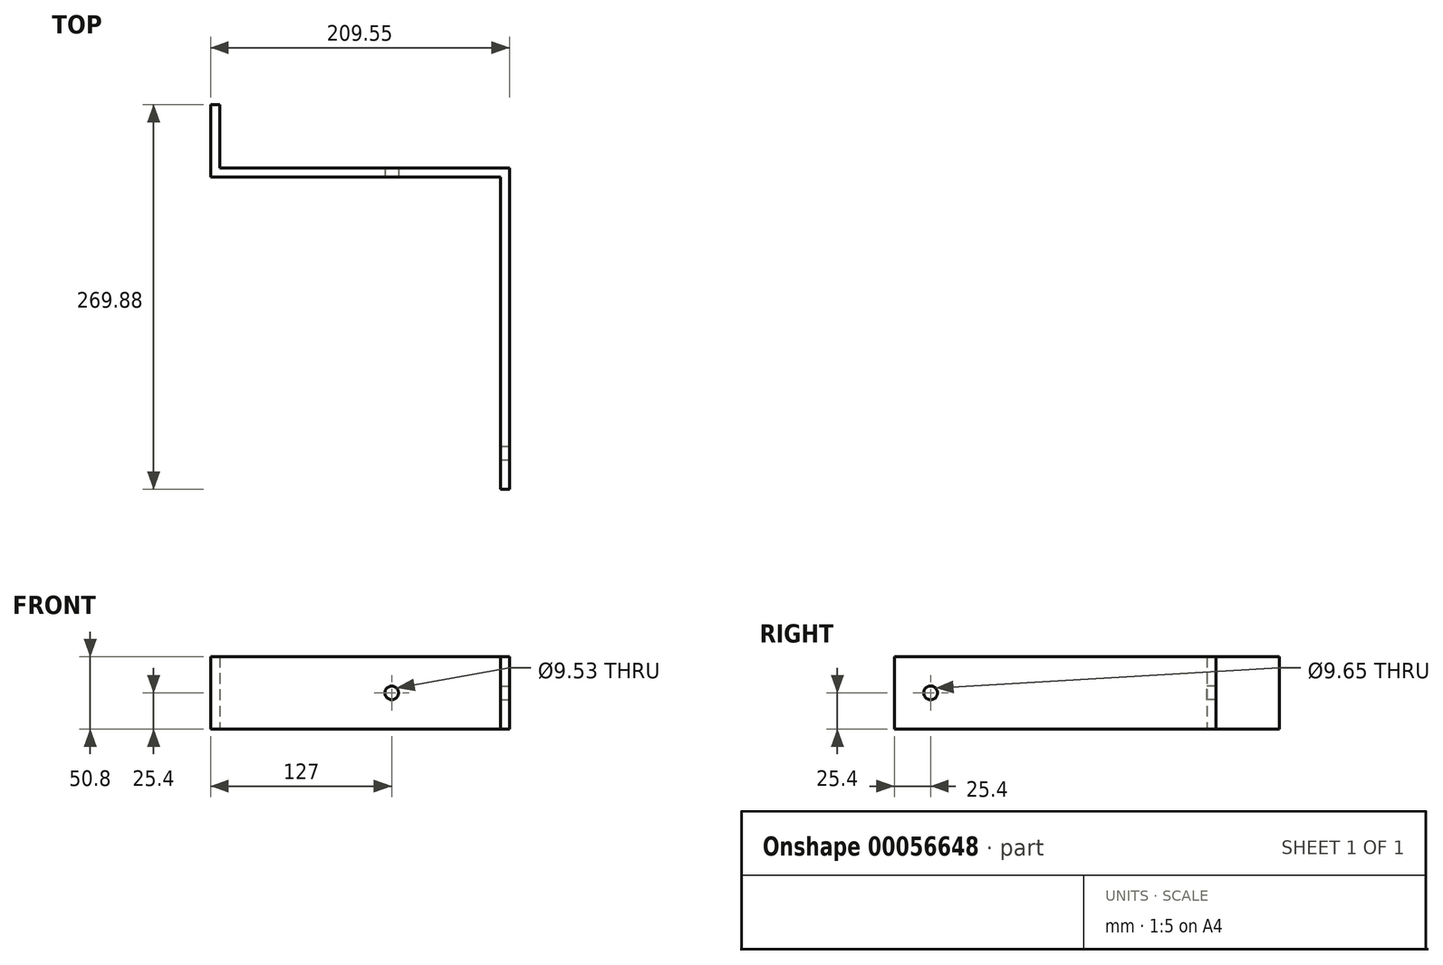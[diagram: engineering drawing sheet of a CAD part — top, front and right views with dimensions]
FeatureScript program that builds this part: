
annotation { "Feature Type Name" : "Feature", "Feature Type Description" : "" }
export const myFeature = defineFeature(function(context is Context, id is Id, definition is map)
    precondition{}
    {
        {
            var Q0;
            Q0=qCreatedBy(makeId("Top.planeOp"),FACE);
            var sketch = newSketch(context, id + "F0", { "sketchPlane" : qUnion([Q0])});
            skLineSegment(sketch, "E0", {"start": v(-6.35, 0) * mm, "end": v(-6.35, 219.08) * mm});
            skLineSegment(sketch, "E1", {"start": v(0, 225.43) * mm, "end": v(0, 0) * mm});
            skLineSegment(sketch, "E2", {"start": v(0, 225.43) * mm, "end": v(-203.2, 225.43) * mm});
            skLineSegment(sketch, "E3", {"start": v(-203.2, 225.42) * mm, "end": v(-203.2, 269.88) * mm});
            skLineSegment(sketch, "E4", {"start": v(-203.2, 269.88) * mm, "end": v(-209.55, 269.88) * mm});
            skLineSegment(sketch, "E5", {"start": v(-209.55, 269.88) * mm, "end": v(-209.55, 219.07) * mm});
            skLineSegment(sketch, "E6", {"start": v(-6.35, 219.08) * mm, "end": v(-209.55, 219.07) * mm});
            skLineSegment(sketch, "E7", {"start": v(-6.35, 0) * mm, "end": v(0, 0) * mm});
            skSolve(sketch);
        }
        {
            var Q0;
            Q0=qSketchRegion(id+"F0",true);
            extrude(context, id + "F1", {"entities" : qUnion([Q0]), "endBound" : BoundingType.SYMMETRIC, "depth" : 50.8 * mm});
        }
        {
            var Q0;
            Q0=makeQuery(id+"F1.opExtrude","SWEPT_FACE",FACE,{"disambiguationData":[OSD([sQuery(id+"F0.wireOp",EDGE,"E6")])]});
            var sketch = newSketch(context, id + "F2", { "sketchPlane" : qUnion([Q0])});
            skCircle(sketch, "E8", {"center": v(-82.55, 0) * mm, "radius": 4.76 * mm});
            skSolve(sketch);
        }
        {
            var Q0;
            Q0=qSketchRegion(id+"F2",true);
            extrude(context, id + "F3", {"entities" : qUnion([Q0]), "operationType" : NewBodyOperationType.REMOVE, "endBound" : BoundingType.THROUGH_ALL, "oppositeDirection" : true, "depth" : 25.4 * mm});
        }
        {
            var Q0;
            Q0=makeQuery(id+"F1.opExtrude","SWEPT_FACE",FACE,{"disambiguationData":[OSD([sQuery(id+"F0.wireOp",EDGE,"E1")])]});
            var sketch = newSketch(context, id + "F4", { "sketchPlane" : qUnion([Q0])});
            skCircle(sketch, "E9", {"center": v(25.4, 0) * mm, "radius": 4.83 * mm});
            skSolve(sketch);
        }
        {
            var Q0;
            Q0 = qSketchRegion(id + "F4", true);
            extrude(context, id + "F5", {"entities" : qUnion([Q0]), "operationType" : NewBodyOperationType.REMOVE, "endBound" : BoundingType.THROUGH_ALL, "oppositeDirection" : true, "depth" : 25.4 * mm});
        }
    });
